# Revit family: Basin-Vanity_Sink-DXV-Belshire-D19085030
name_source: partatom
category: Plumbing Fixtures
revit_build: Autodesk Revit 2018 (Build: 20170223_1515(x64)
units: mm (PartAtom-declared; Revit-internal decimal feet)

## family parameters
Always vertical = Yes
Cut with Voids When Loaded = No
OmniClass Number = 23.45.05.14.14
OmniClass Title = Sinks/Lavatories
Part Type = Normal
Room Calculation Point = No
Round Connector Dimension = Use Diameter
Shared = Yes
Work Plane-Based = No

## types (1)
- D19085030.414
    Assembly Code = D2010400
    Basin Shape = Rectangular
    CW Connection = Yes
    CWFU = 1.5
    Cold Water Connection Diameter = 1/2"
    Cold Water Connection Radius = 1/4"
    Countertop Finish = Marble-DXV-550-Carrara
    Description = DXV BELSHIRE™ NATURAL OAK VANITY
    HW Connection = Yes
    HWFU = 1.5
    Height = 36 3/16"
    Hot Water Connection Diameter = 1/2"
    Hot Water Connection Radius = 1/4"
    Installation Type = Floor Mounted
    Length = 22 1/2"
    Manufacturer = DXV
    Model = D19085030.414
    Price = Prices may vary. Please consult Manufacturer Representative for most up-to-date price list.
    Product Documentation Link = https://dxv01.blob.core.windows.net
    Product Page URL = https://www.dxv.com
    Revised Date = 04/05/2021
    URL = https://www.dxv.com
    Vanity Finish = Wood_DXV-414-Natural_Oak
    Vanity Leg Set Finish = Metal-DXV-150-Platinum_Nickel
    Vent Connection = No
    WFU = 2
    Warranty Documentation Link = https://www.dxv.com
    Waste Connection = Yes
    Waste Connection Diameter = 1 1/4"
    Width = 30"

## geometry (parser evidence)
native form markers: Sweep x4
no freeform markers — native parametric forms only
